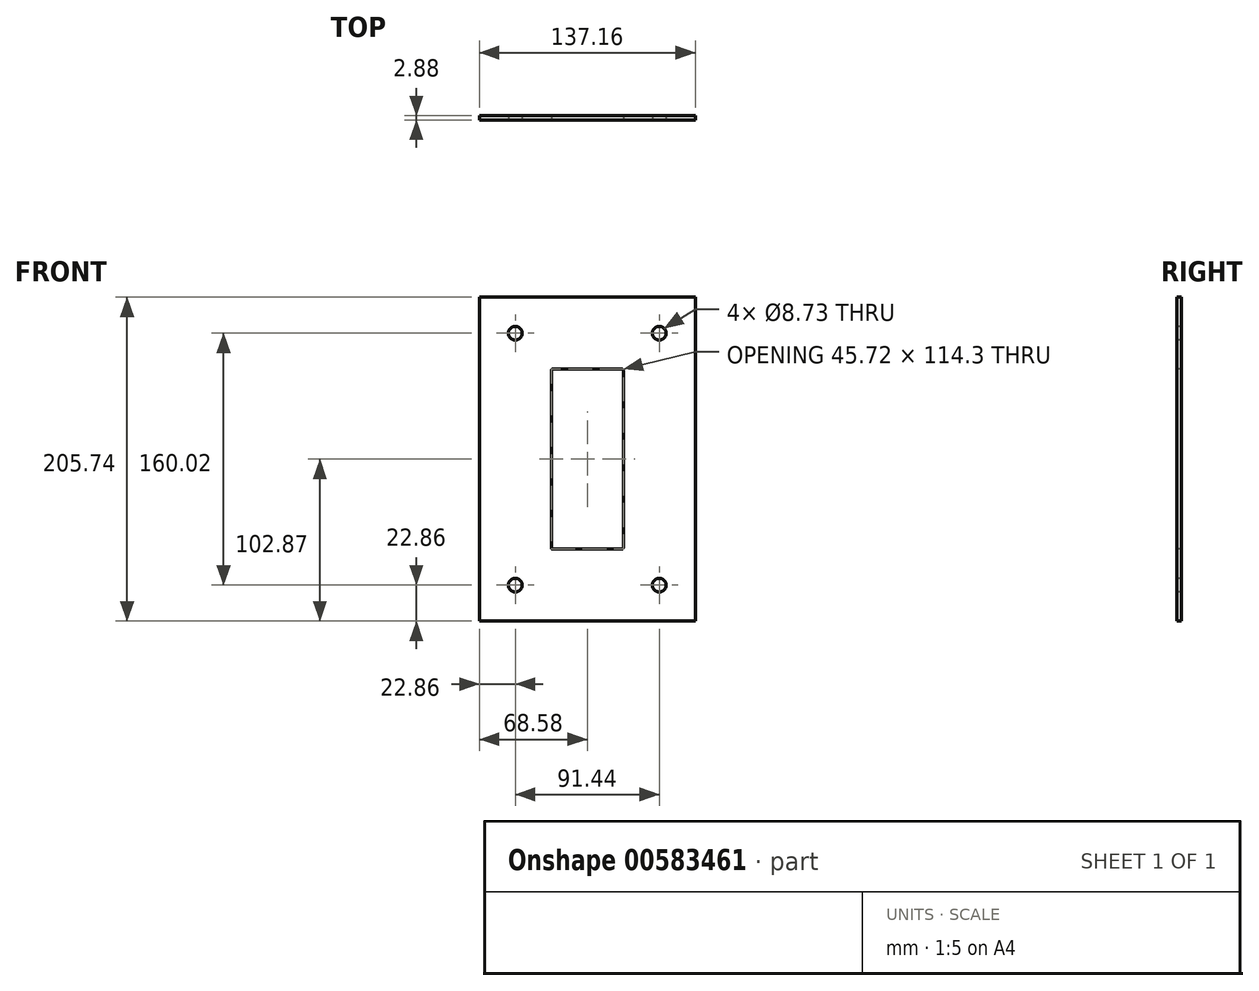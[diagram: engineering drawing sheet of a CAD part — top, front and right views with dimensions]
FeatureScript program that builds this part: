
annotation { "Feature Type Name" : "Feature", "Feature Type Description" : "" }
export const myFeature = defineFeature(function(context is Context, id is Id, definition is map)
    precondition{}
    {
        {
            assignVariable(context, id + "F0", {"name" : "StackHeight", "anyValue" : 2.88});
        }
        {
            var Q0;
            Q0=qCreatedBy(makeId("Front.planeOp"),FACE);
            var sketch = newSketch(context, id + "F1", { "sketchPlane" : qUnion([Q0])});
            skLineSegment(sketch, "E0.bottom", {"start": v(68.58, -102.87) * mm, "end": v(-68.58, -102.87) * mm});
            skLineSegment(sketch, "E0.top", {"start": v(68.58, 102.87) * mm, "end": v(-68.58, 102.87) * mm});
            skLineSegment(sketch, "E0.left", {"start": v(68.58, -102.87) * mm, "end": v(68.58, 102.87) * mm});
            skLineSegment(sketch, "E0.right", {"start": v(-68.58, -102.87) * mm, "end": v(-68.58, 102.87) * mm});
            skPoint(sketch, "E0.middle", {"position": v(0, 0) * mm});
            skSolve(sketch);
        }
        {
            var Q0;
            Q0=qSketchRegion(id+"F1",true);
            extrude(context, id + "F2", {"entities" : qUnion([Q0]), "oppositeDirection" : true, "depth" : (getVariable(context, 'StackHeight')) * mm});
        }
        {
            var Q0;
            Q0=makeQuery(id+"F2.opExtrude","CAP_FACE",FACE,{"disambiguationData":[OSD([sQuery(id+"F1.wireOp",EDGE,"E0.bottom"),sQuery(id+"F1.wireOp",EDGE,"E0.top"),sQuery(id+"F1.wireOp",EDGE,"E0.left"),sQuery(id+"F1.wireOp",EDGE,"E0.right")])],"isStart":true});
            var sketch = newSketch(context, id + "F3", { "sketchPlane" : qUnion([Q0])});
            skCircle(sketch, "E1", {"center": v(-45.72, 80.01) * mm, "radius": 4.37 * mm});
            skCircle(sketch, "E2", {"center": v(45.72, 80.01) * mm, "radius": 4.37 * mm});
            skCircle(sketch, "E3", {"center": v(-45.72, -80) * mm, "radius": 4.37 * mm});
            skCircle(sketch, "E4", {"center": v(45.72, -80) * mm, "radius": 4.37 * mm});
            skSolve(sketch);
        }
        {
            var Q0;
            Q0=qSketchRegion(id+"F3",true);
            extrude(context, id + "F4", {"entities" : qUnion([Q0]), "operationType" : NewBodyOperationType.REMOVE, "oppositeDirection" : true, "depth" : (getVariable(context, 'StackHeight')) * mm});
        }
        {
            var Q0;
            Q0=makeQuery(id+"F2.opExtrude","CAP_FACE",FACE,{"disambiguationData":[OSD([sQuery(id+"F1.wireOp",EDGE,"E0.bottom"),sQuery(id+"F1.wireOp",EDGE,"E0.top"),sQuery(id+"F1.wireOp",EDGE,"E0.left"),sQuery(id+"F1.wireOp",EDGE,"E0.right")])],"isStart":true});
            var sketch = newSketch(context, id + "F5", { "sketchPlane" : qUnion([Q0])});
            skLineSegment(sketch, "E5.bottom", {"start": v(-22.86, -57.15) * mm, "end": v(22.86, -57.15) * mm});
            skLineSegment(sketch, "E5.top", {"start": v(-22.86, 57.15) * mm, "end": v(22.86, 57.15) * mm});
            skLineSegment(sketch, "E5.left", {"start": v(-22.86, -57.15) * mm, "end": v(-22.86, 57.15) * mm});
            skLineSegment(sketch, "E5.right", {"start": v(22.86, -57.15) * mm, "end": v(22.86, 57.15) * mm});
            skPoint(sketch, "E5.middle", {"position": v(0, 0) * mm});
            skSolve(sketch);
        }
        {
            var Q0;
            Q0=qSketchRegion(id+"F5",true);
            extrude(context, id + "F6", {"entities" : qUnion([Q0]), "operationType" : NewBodyOperationType.REMOVE, "oppositeDirection" : true, "depth" : (getVariable(context, 'StackHeight')) * mm});
        }
        {
            var Q0;
            Q0=makeQuery(id+"F6.boolean.opBoolean","COPY",EDGE,{"derivedFrom":makeQuery(id+"F6.opExtrude","SWEPT_EDGE",EDGE,{"disambiguationData":[OSD([sQuery(id+"F5.wireOp",EDGE,"E5.top"),sQuery(id+"F5.wireOp",EDGE,"E5.left")])]})});
            var Q1;
            Q1=makeQuery(id+"F6.boolean.opBoolean","COPY",EDGE,{"derivedFrom":makeQuery(id+"F6.opExtrude","SWEPT_EDGE",EDGE,{"disambiguationData":[OSD([sQuery(id+"F5.wireOp",EDGE,"E5.top"),sQuery(id+"F5.wireOp",EDGE,"E5.right")])]})});
            var Q2;
            Q2=makeQuery(id+"F6.boolean.opBoolean","COPY",EDGE,{"derivedFrom":makeQuery(id+"F6.opExtrude","SWEPT_EDGE",EDGE,{"disambiguationData":[OSD([sQuery(id+"F5.wireOp",EDGE,"E5.bottom"),sQuery(id+"F5.wireOp",EDGE,"E5.right")])]})});
            var Q3;
            Q3=makeQuery(id+"F6.boolean.opBoolean","COPY",EDGE,{"derivedFrom":makeQuery(id+"F6.opExtrude","SWEPT_EDGE",EDGE,{"disambiguationData":[OSD([sQuery(id+"F5.wireOp",EDGE,"E5.bottom"),sQuery(id+"F5.wireOp",EDGE,"E5.left")])]})});
            fillet(context, id + "F7", {"entities" : qUnion([Q0, Q1, Q2, Q3]), "radius" : 0.8 * mm, "tangentPropagation" : true, "allowEdgeOverflow" : false});
        }
    });
